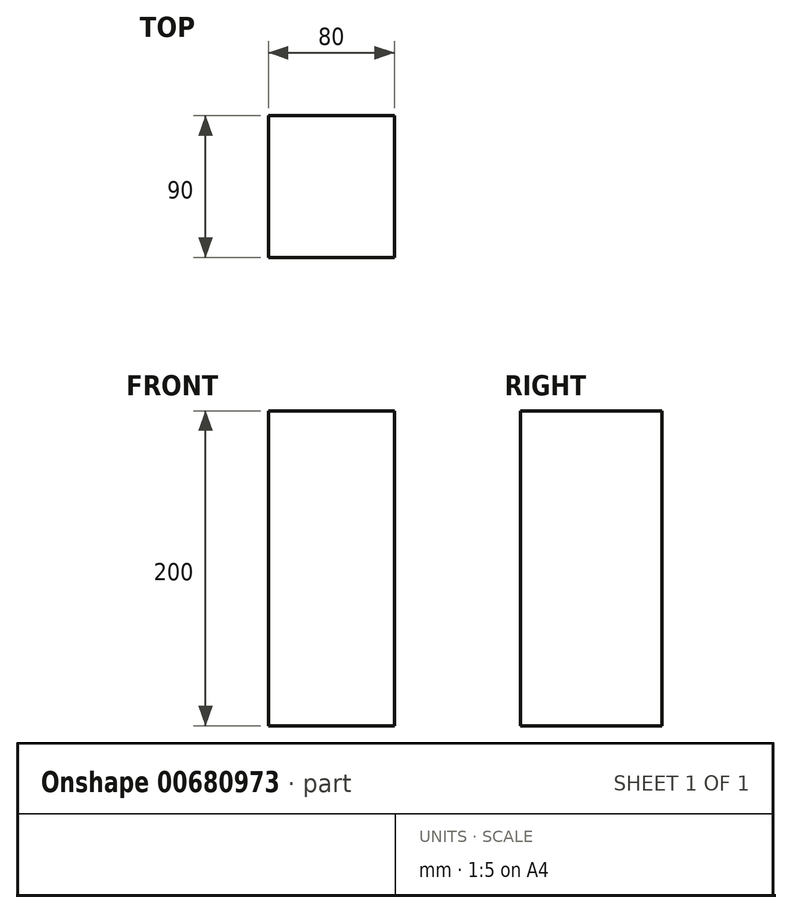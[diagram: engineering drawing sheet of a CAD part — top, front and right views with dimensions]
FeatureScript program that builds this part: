
annotation { "Feature Type Name" : "Feature", "Feature Type Description" : "" }
export const myFeature = defineFeature(function(context is Context, id is Id, definition is map)
    precondition{}
    {
        {
            var Q0;
            Q0=qCreatedBy(makeId("Top.planeOp"),FACE);
            var sketch = newSketch(context, id + "F0", { "sketchPlane" : qUnion([Q0])});
            skLineSegment(sketch, "E0", {"start": v(-38.53, 36.96) * mm, "end": v(41.47, 36.96) * mm});
            skLineSegment(sketch, "E1", {"start": v(41.47, 36.96) * mm, "end": v(41.47, -53.04) * mm});
            skLineSegment(sketch, "E2", {"start": v(41.47, -53.04) * mm, "end": v(-38.53, -53.04) * mm});
            skLineSegment(sketch, "E3", {"start": v(-38.53, -53.04) * mm, "end": v(-38.53, 36.96) * mm});
            skSolve(sketch);
        }
        {
            var Q0;
            Q0 = qSketchRegion(id + "F0", true);
            extrude(context, id + "F1", {"entities" : qUnion([Q0]), "depth" : 200 * mm, "offsetDistance" : 25 * mm});
        }
    });
